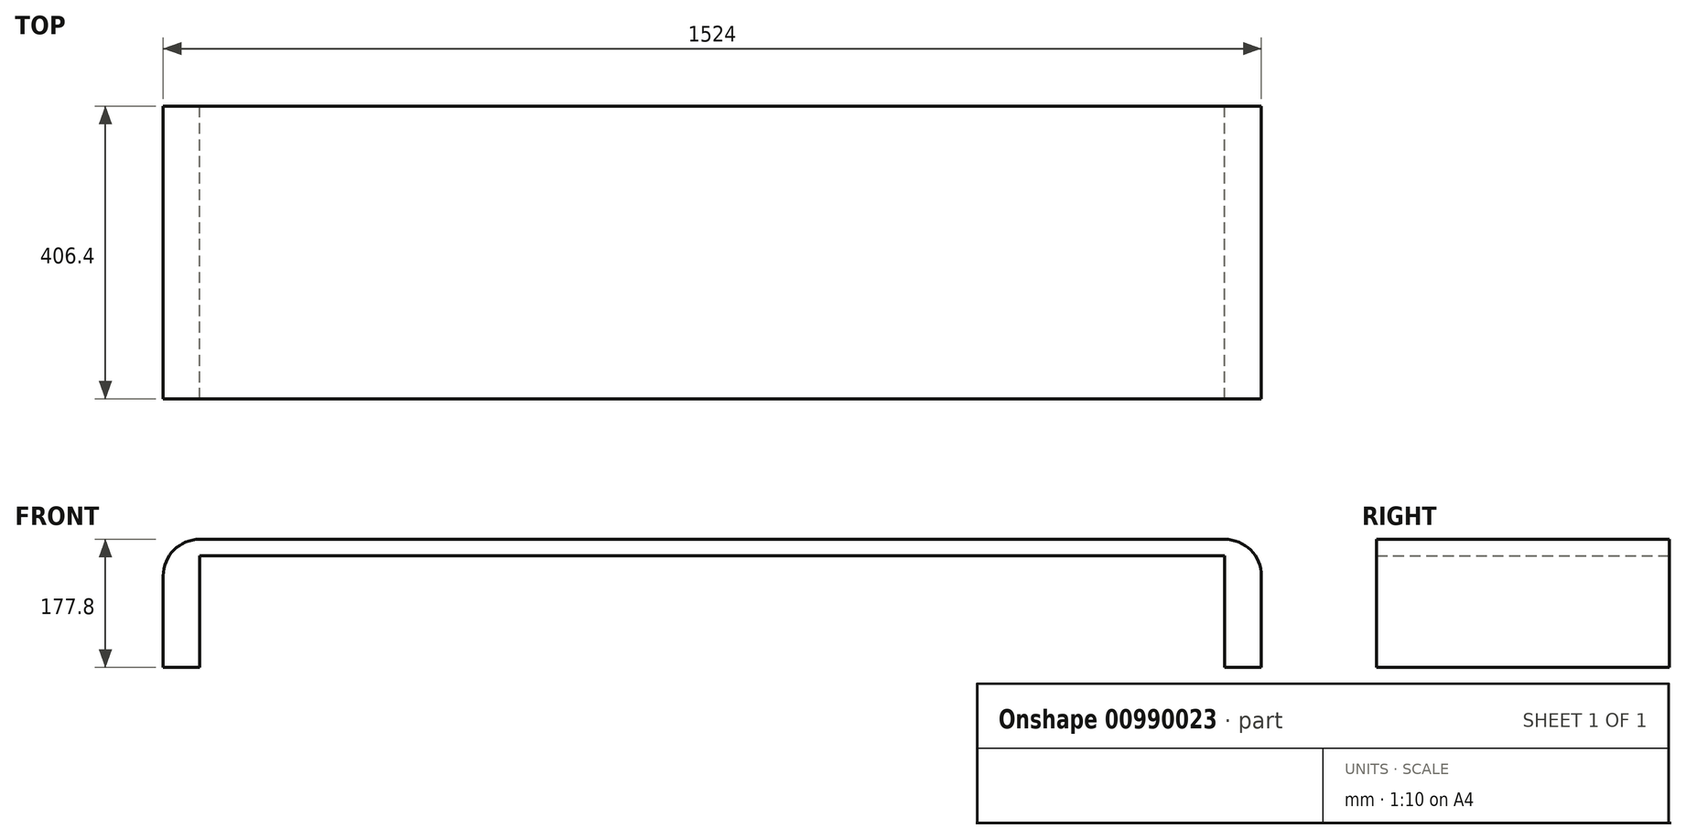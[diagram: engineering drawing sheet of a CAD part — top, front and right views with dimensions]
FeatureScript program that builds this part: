
annotation { "Feature Type Name" : "Feature", "Feature Type Description" : "" }
export const myFeature = defineFeature(function(context is Context, id is Id, definition is map)
    precondition{}
    {
        {
            var Q0;
            Q0=qCreatedBy(makeId("Front.planeOp"),FACE);
            var sketch = newSketch(context, id + "F0", { "sketchPlane" : qUnion([Q0])});
            skLineSegment(sketch, "E0", {"start": v(0, 0) * mm, "end": v(-50.8, 0) * mm});
            skLineSegment(sketch, "E1", {"start": v(0, 0) * mm, "end": v(0, 154.94) * mm});
            skLineSegment(sketch, "E2", {"start": v(-50.8, 0) * mm, "end": v(-50.8, 177.8) * mm});
            skPoint(sketch, "E3.end.orphan", {"position": v(390, 0) * mm});
            skPoint(sketch, "E3.start.orphan", {"position": v(380, 0) * mm});
            skLineSegment(sketch, "E4", {"start": v(0, 154.94) * mm, "end": v(1422.4, 154.94) * mm});
            skLineSegment(sketch, "E5", {"start": v(-50.8, 177.8) * mm, "end": v(1473.2, 177.8) * mm});
            skLineSegment(sketch, "E6", {"start": v(1473.2, 177.8) * mm, "end": v(1473.2, 0) * mm});
            skLineSegment(sketch, "E7", {"start": v(1422.4, 154.94) * mm, "end": v(1422.4, 0) * mm});
            skLineSegment(sketch, "E8", {"start": v(1422.4, 0) * mm, "end": v(1473.2, 0) * mm});
            skSolve(sketch);
        }
        {
            var Q0;
            Q0=qSketchRegion(id+"F0",true);
            extrude(context, id + "F1", {"entities" : qUnion([Q0]), "depth" : 406.4 * mm});
        }
        {
            var Q0;
            Q0=makeQuery(id+"F1.opExtrude","SWEPT_EDGE",EDGE,{"disambiguationData":[OSD([sQuery(id+"F0.wireOp",EDGE,"E5"),sQuery(id+"F0.wireOp",EDGE,"E6")])]});
            var Q1;
            Q1=makeQuery(id+"F1.opExtrude","SWEPT_EDGE",EDGE,{"disambiguationData":[OSD([sQuery(id+"F0.wireOp",EDGE,"E2"),sQuery(id+"F0.wireOp",EDGE,"E5")])]});
            fillet(context, id + "F2", {"entities" : qUnion([Q0, Q1]), "radius" : 50.8 * mm, "tangentPropagation" : true, "allowEdgeOverflow" : false});
        }
    });
